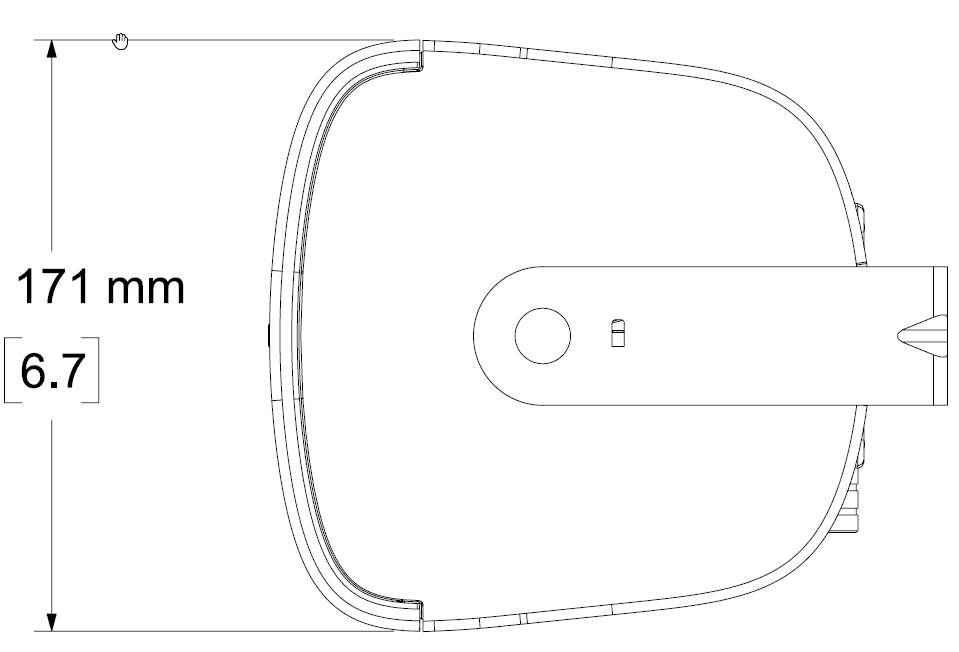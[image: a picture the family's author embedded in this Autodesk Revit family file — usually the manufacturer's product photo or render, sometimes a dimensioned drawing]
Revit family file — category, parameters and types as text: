
# Revit family: Electronics_Loudspeaker_Bose-Professional_Designmax_FS4SE
name_source: partatom
category: Communication Devices
units: mm (PartAtom-declared; Revit-internal decimal feet)

## family parameters
Cut with Voids When Loaded = No
Host = Face
Maintain Annotation Orientation = No
OmniClass Number = 23.85.10.11.14.14.14
OmniClass Title = Loudspeakers
Part Type = Normal
Room Calculation Point = No
Round Connector Dimension = Use Diameter
Shared = No

## types (2) — shared parameters
Assembly Code = D5030
Default Elevation = 1219 mm
Depth = 174 mm
Description = Premium sound to maximize any design.
DesignMax loudspeakers bring outstanding audio and aesthetics to any commercial space. With 12 models to choose from, it’s easy to create tailored solutions that deliver instantly impressive sound. QuickHold mounting mechanisms make installation efficient, reducing strain and hassle — and saving substantial time. And with both black and white versions available, DesignMax loudspeakers integrate seamlessly with any décor.

The 50-watt DesignMax DM5SE loudspeaker features a two-way 5.25-inch woofer and 1-inch tweeter coaxially mounted within the Dispersion Alignment system, producing a frequency range of 60 Hz - 20 kHz. The DM5SE is surface-mounted, IP55 outdoor-rated, and locks onto a hidden QuickHold U-bracket for fast, secure installation. 

FEATURES
Combine models to complete any design, big or small — 12 loudspeakers to mix and match, from 2-inch, low-profile models to 8-inch, high-SPL compression-driver loudspeakers and outdoor-rated options

Deliver instantly impressive sound with custom Bose drivers — no DSP or EQ required. For even better sound, use select Bose DSPs and amplifiers to enable Bose loudspeaker EQ and SmartBass processing, which expands performance and response at any listening level

Ensure a consistent listening experience throughout the room with the Dispersion Alignment system, which matches the coverage of the woofer to the pattern of the tweeter

Reduce installation time with the patented QuickHold mounting system, which also reduces strain, hassle, and the chance of product damage

Install easily — all models include Euroblock connectors; ceiling-mounted models include plenum-rated backcans, tile-bridges, and front-access audio wiring that makes installation and troubleshooting easier

Install DM5SE outside — IP55 rating with standard aluminum grille for outdoor use 

Applications
Performing arts venues
Places of worship
Conference centers
Retail stores
Restaurants and bars
Hospitality venues
Edition number = 1
Environmental = Rated for direct-exposure outdoor installations (IP55 per EN60529; IP33C per EN54-24). Suitable for use outdoors in wet locations. Includes weather-resistant input cover. Optional accessory aluminum grille for harsh environments to prevent red corrosion is available.
Frequency Range = 80 - 16,000 Hz
Frequency Response = 70 – 17,000 Hz
Full-Range Driver = 1 × 4.5-inch woofer (114 mm)
Height = 254 mm
Keynote = 16700
Manufacturer = Bose Professional
Material = Metal-Bose-Aluminium
Model = DesignMax DM5SE
Mounting/Suspension = External U-bracket with bracket screws
7 preset mounting angles: 0°, +15°, +30°, or +45° for wall or ceiling placement
Two (2) rear M8 screw inserts for use with optional Ceiling Mount Bracket S2,
WBPWR-50 pan-and-tilt bracket (for outdoors), or RMUBRKT1 pan-and-tilt
bracket (for indoors)
Safety cable can be used with either of two (2) rear M8 inserts when using included U-bracket,
or with either of two (2) side M8 inserts, when using optional brackets
Nominal Coverage Pattern = 130° × 125°
Nominal Impedance = 8 Ω (transformer bypass)
Nominal Sensitivity = 89 dB
Operating Temperature Range = -25 to 70 °C (-13 °F to 158 °F)
Power Connector = Euroblock 6-pin connector with loop-through, mounted on rear. Accepts 18 AWG (0.8 mm2) to 14 AWG (2.5 mm2) size wire
Power Handling(Long-term continuous) = 50 W
Power Handling(peak) = 200 W
Product Guid = cc3887de-f3d8-414a-8418-c141068ee284
Product code = 829705-0210
Product data url = https://www.bimobject.com
Rated Maximum SPL = 106 dB
Recommended High-pass Filter = 70 Hz with recommended 24 dB / octave filter
Transformer Taps Information = 70V: 2.5, 5, 10, 20, 40 W, bypass  100V:5, 10, 20, 40 W, bypass
URL = https://www.bose.com
Weight = 3.08 kg
Width = 171 mm

## per-type parameters (varying)
| type | Bracket Material | Mesh Material | Speaker Material |
| FS4SE-White | Metal-Bose-Aluminium | Grill-Bose-White | Metal-Bose-White |
| FS4SE-Black | Metal-Bose-Black | Grill-Bose-Black | Metal-Bose-Black |

## geometry (parser evidence)
native form markers: Sweep x11
no freeform markers — native parametric forms only
